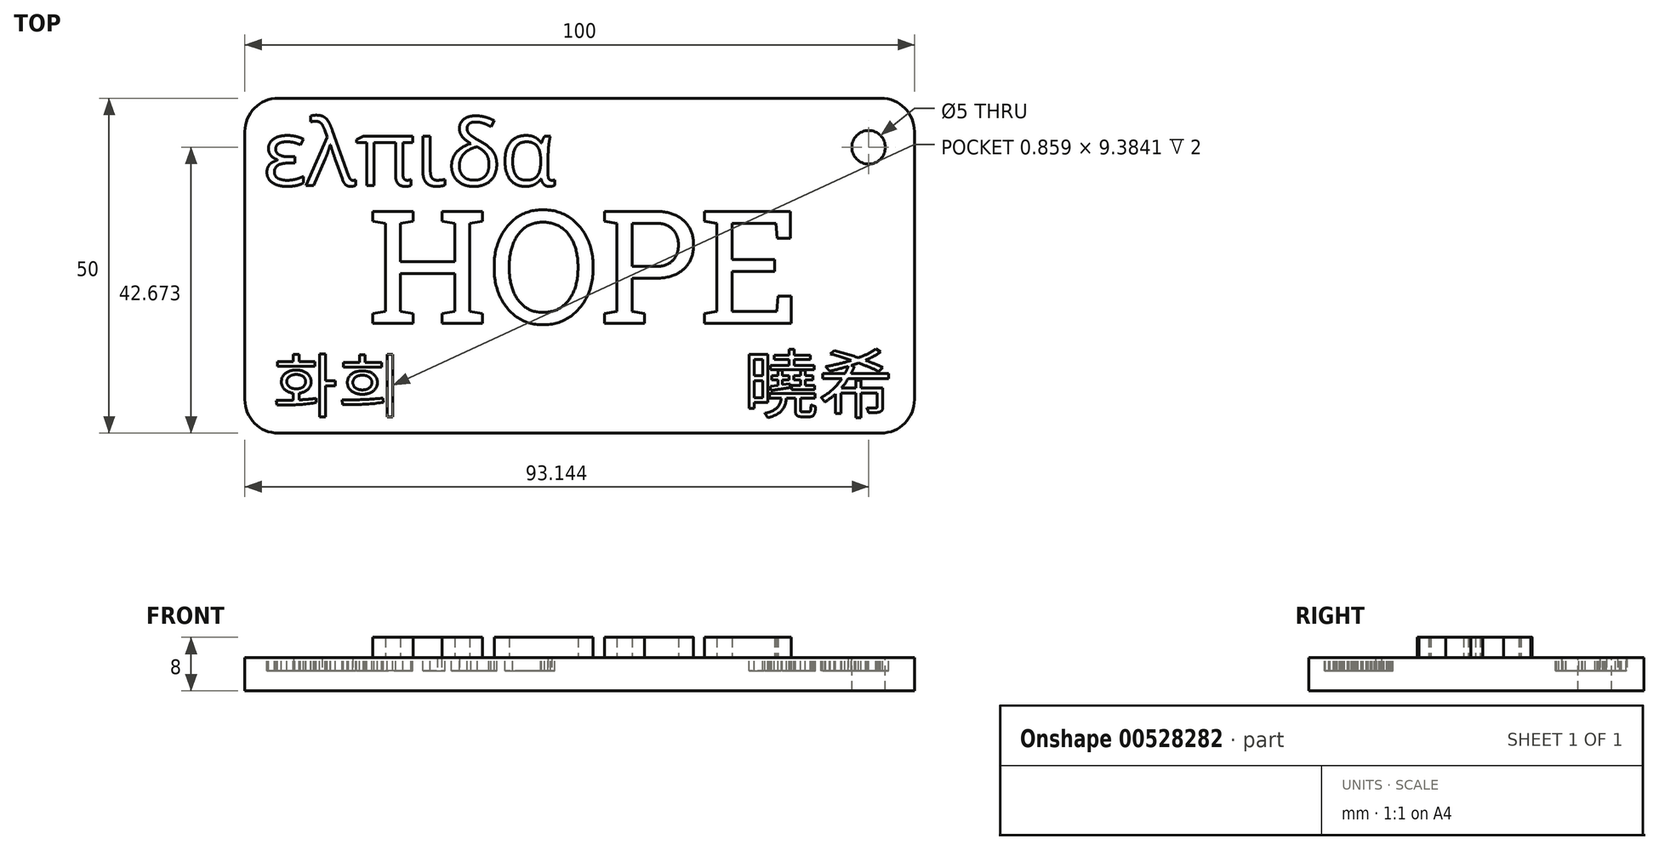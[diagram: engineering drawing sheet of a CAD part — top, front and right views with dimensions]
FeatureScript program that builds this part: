
annotation { "Feature Type Name" : "Feature", "Feature Type Description" : "" }
export const myFeature = defineFeature(function(context is Context, id is Id, definition is map)
    precondition{}
    {
        {
            var Q0;
            Q0=qCreatedBy(makeId("Top.planeOp"),FACE);
            var sketch = newSketch(context, id + "F0", { "sketchPlane" : qUnion([Q0])});
            skLineSegment(sketch, "E0.bottom", {"start": v(50, 25) * mm, "end": v(-50, 25) * mm});
            skLineSegment(sketch, "E0.top", {"start": v(50, -25) * mm, "end": v(-50, -25) * mm});
            skLineSegment(sketch, "E0.left", {"start": v(50, 25) * mm, "end": v(50, -25) * mm});
            skLineSegment(sketch, "E0.right", {"start": v(-50, 25) * mm, "end": v(-50, -25) * mm});
            skPoint(sketch, "E0.middle", {"position": v(0, 0) * mm});
            skSolve(sketch);
        }
        {
            var Q0;
            Q0=makeQuery(id+"F0.imprint","IMPRINT",FACE,{"disambiguationData":[TD([[makeQuery(id+"F0.imprint","IMPRINT",EDGE,{"derivedFrom":sQuery(id+"F0.wireOp",EDGE,"E0.bottom")}),1.0]])]});
            extrude(context, id + "F1", {"entities" : qUnion([Q0]), "depth" : 5 * mm, "offsetDistance" : 25 * mm});
        }
        {
            var Q0;
            Q0=makeQuery(id+"F1.opExtrude","CAP_FACE",FACE,{"disambiguationData":[OSD([sQuery(id+"F0.wireOp",EDGE,"E0.bottom"),sQuery(id+"F0.wireOp",EDGE,"E0.top"),sQuery(id+"F0.wireOp",EDGE,"E0.left"),sQuery(id+"F0.wireOp",EDGE,"E0.right")])],"isStart":false});
            var sketch = newSketch(context, id + "F2", { "sketchPlane" : qUnion([Q0])});
            skText(sketch, "E1", { "text": "HOPE", "fontName": "RobotoSlab-Regular.ttf"});
            const initialGuessF2  = {"E1": [-0.0317, -0.00858, 1, 0, 0.0169]};
            skSetInitialGuess(sketch, initialGuessF2);
            skSolve(sketch);
        }
        {
            var Q0;
            Q0 = qSketchRegion(id + "F2", true);
            extrude(context, id + "F3", {"entities" : qUnion([Q0]), "operationType" : NewBodyOperationType.ADD, "depth" : 3 * mm, "offsetDistance" : 25 * mm});
        }
        {
            var Q0;
            {var subQ0=sQuery(id+"F0.wireOp",EDGE,"E0.left");var subQ1=sQuery(id+"F0.wireOp",EDGE,"E0.bottom");var subQ2=sQuery(id+"F0.wireOp",EDGE,"E0.right");var subQ3=sQuery(id+"F0.wireOp",EDGE,"E0.top");Q0=makeQuery(id+"F3.boolean.opBoolean","SPLIT",FACE,{"disambiguationData":[TD([makeQuery(id+"F1.opExtrude","SWEPT_FACE",FACE,{"disambiguationData":[OSD([subQ1])]})])],"derivedFrom":makeQuery(id+"F1.opExtrude","CAP_FACE",FACE,{"disambiguationData":[OSD([subQ1,subQ3,subQ0,subQ2])],"isStart":false})});}
            var sketch = newSketch(context, id + "F4", { "sketchPlane" : qUnion([Q0])});
            skText(sketch, "E2", { "text": "화희", "fontName": "NotoSansCJKkr-Regular.otf"});
            const initialGuessF4  = {"E2": [-0.04574, -0.02183, 1, 0, 0.00754]};
            skSetInitialGuess(sketch, initialGuessF4);
            skSolve(sketch);
        }
        {
            var Q0;
            Q0 = qSketchRegion(id + "F4", true);
            extrude(context, id + "F5", {"entities" : qUnion([Q0]), "operationType" : NewBodyOperationType.REMOVE, "oppositeDirection" : true, "depth" : 2 * mm, "offsetDistance" : 25 * mm});
        }
        {
            var Q0;
            {var subQ42=sQuery(id+"F0.wireOp",EDGE,"E0.top");var subQ46=sQuery(id+"F0.wireOp",EDGE,"E0.right");var subQ53=sQuery(id+"F0.wireOp",EDGE,"E0.bottom");var subQ54=makeQuery(id+"F1.opExtrude","SWEPT_FACE",FACE,{"disambiguationData":[OSD([subQ53])]});var subQ56=sQuery(id+"F0.wireOp",EDGE,"E0.left");Q0=makeQuery(id+"F5.boolean.opBoolean","SPLIT",FACE,{"disambiguationData":[TD([subQ54])],"derivedFrom":makeQuery(id+"F3.boolean.opBoolean","SPLIT",FACE,{"disambiguationData":[TD([subQ54])],"derivedFrom":makeQuery(id+"F1.opExtrude","CAP_FACE",FACE,{"disambiguationData":[OSD([subQ53,subQ42,subQ56,subQ46])],"isStart":false})})});}
            var sketch = newSketch(context, id + "F6", { "sketchPlane" : qUnion([Q0])});
            skText(sketch, "E3", { "text": "曉希", "fontName": "NotoSansCJKtc-Regular.otf"});
            const initialGuessF6  = {"E3": [0.02443, -0.02183, 1, 0, 0.00806]};
            skSetInitialGuess(sketch, initialGuessF6);
            skSolve(sketch);
        }
        {
            var Q0;
            Q0 = qSketchRegion(id + "F6", true);
            extrude(context, id + "F7", {"entities" : qUnion([Q0]), "operationType" : NewBodyOperationType.REMOVE, "oppositeDirection" : true, "depth" : 2 * mm, "offsetDistance" : 25 * mm});
        }
        {
            var Q0;
            {var subQ0=sQuery(id+"F0.wireOp",EDGE,"E0.bottom");var subQ1=makeQuery(id+"F1.opExtrude","SWEPT_FACE",FACE,{"disambiguationData":[OSD([subQ0])]});var subQ49=sQuery(id+"F0.wireOp",EDGE,"E0.left");var subQ58=sQuery(id+"F0.wireOp",EDGE,"E0.right");var subQ63=sQuery(id+"F0.wireOp",EDGE,"E0.top");Q0=makeQuery(id+"F7.boolean.opBoolean","SPLIT",FACE,{"disambiguationData":[TD([subQ1])],"derivedFrom":makeQuery(id+"F5.boolean.opBoolean","SPLIT",FACE,{"disambiguationData":[TD([subQ1])],"derivedFrom":makeQuery(id+"F3.boolean.opBoolean","SPLIT",FACE,{"disambiguationData":[TD([subQ1])],"derivedFrom":makeQuery(id+"F1.opExtrude","CAP_FACE",FACE,{"disambiguationData":[OSD([subQ0,subQ63,subQ49,subQ58])],"isStart":false})})})});}
            var sketch = newSketch(context, id + "F8", { "sketchPlane" : qUnion([Q0])});
            skText(sketch, "E4", { "text": "ελπιδα", "fontName": "OpenSans-Regular.ttf"});
            const initialGuessF8  = {"E4": [-0.0473, 0.01196, 1, 0, 0.00988]};
            skSetInitialGuess(sketch, initialGuessF8);
            skSolve(sketch);
        }
        {
            var Q0;
            Q0 = qSketchRegion(id + "F8", true);
            extrude(context, id + "F9", {"entities" : qUnion([Q0]), "operationType" : NewBodyOperationType.REMOVE, "oppositeDirection" : true, "depth" : 2 * mm, "offsetDistance" : 25 * mm});
        }
        {
            var Q0;
            Q0=makeQuery(id+"F1.opExtrude","SWEPT_EDGE",EDGE,{"disambiguationData":[OSD([sQuery(id+"F0.wireOp",EDGE,"E0.top"),sQuery(id+"F0.wireOp",EDGE,"E0.right")])]});
            var Q1;
            Q1=makeQuery(id+"F1.opExtrude","SWEPT_EDGE",EDGE,{"disambiguationData":[OSD([sQuery(id+"F0.wireOp",EDGE,"E0.top"),sQuery(id+"F0.wireOp",EDGE,"E0.left")])]});
            var Q2;
            Q2=makeQuery(id+"F1.opExtrude","SWEPT_EDGE",EDGE,{"disambiguationData":[OSD([sQuery(id+"F0.wireOp",EDGE,"E0.bottom"),sQuery(id+"F0.wireOp",EDGE,"E0.left")])]});
            var Q3;
            Q3=makeQuery(id+"F1.opExtrude","SWEPT_EDGE",EDGE,{"disambiguationData":[OSD([sQuery(id+"F0.wireOp",EDGE,"E0.bottom"),sQuery(id+"F0.wireOp",EDGE,"E0.right")])]});
            fillet(context, id + "F10", {"entities" : qUnion([Q0, Q1, Q2, Q3]), "radius" : 5 * mm, "tangentPropagation" : true, "allowEdgeOverflow" : false});
        }
        {
            var Q0;
            {var subQ147=sQuery(id+"F0.wireOp",EDGE,"E0.left");var subQ154=sQuery(id+"F0.wireOp",EDGE,"E0.bottom");var subQ155=makeQuery(id+"F1.opExtrude","SWEPT_FACE",FACE,{"disambiguationData":[OSD([subQ154])]});var subQ163=sQuery(id+"F0.wireOp",EDGE,"E0.right");var subQ171=sQuery(id+"F0.wireOp",EDGE,"E0.top");Q0=makeQuery(id+"F9.boolean.opBoolean","SPLIT",FACE,{"disambiguationData":[TD([subQ155])],"derivedFrom":makeQuery(id+"F7.boolean.opBoolean","SPLIT",FACE,{"disambiguationData":[TD([subQ155])],"derivedFrom":makeQuery(id+"F5.boolean.opBoolean","SPLIT",FACE,{"disambiguationData":[TD([subQ155])],"derivedFrom":makeQuery(id+"F3.boolean.opBoolean","SPLIT",FACE,{"disambiguationData":[TD([subQ155])],"derivedFrom":makeQuery(id+"F1.opExtrude","CAP_FACE",FACE,{"disambiguationData":[OSD([subQ154,subQ171,subQ147,subQ163])],"isStart":false})})})})});}
            var sketch = newSketch(context, id + "F11", { "sketchPlane" : qUnion([Q0])});
            skPoint(sketch, "E5", {"position": v(43.14, 17.67) * mm});
            skSolve(sketch);
        }
        {
            var Q0;
            Q0=sQuery(id+"F11.wireOp",VERTEX,"E5");
            var Q1;
            Q1=makeQuery(id+"F1.opExtrude","SWEPT_BODY",BODY,{"disambiguationData":[OSD([sQuery(id+"F0.wireOp",EDGE,"E0.bottom"),sQuery(id+"F0.wireOp",EDGE,"E0.top"),sQuery(id+"F0.wireOp",EDGE,"E0.left"),sQuery(id+"F0.wireOp",EDGE,"E0.right")])]});
            hole(context, id + "F12", {"style" : HoleStyle.SIMPLE, "endStyle" : HoleEndStyle.THROUGH, "holeDiameter" : 5 * mm, "isTappedThrough" : true, "tappedDepth" : 12 * mm, "tapClearance" : 3, "locations" : qUnion([Q0]), "scope" : qUnion([Q1])});
        }
    });
